# Revit family: BoelsRental_ScissorLift_JLG_1930ESa
name_source: partatom
category: Site
units: mm (PartAtom-declared; Revit-internal decimal feet)

## family parameters
Always vertical = Yes
Cut with Voids When Loaded = No
OmniClass Number = 23.50.05.14.11
OmniClass Title = Scissors Lifts
Part Type = Normal
Round Connector Dimension = Use Diameter
Shared = No
Work Plane-Based = No

## types (1)
- 1930ES
    Assembly Code = E1030100
    AssetType = Movable
    BIMObjectName = BoelsRental_ScissorLift_JLG_1930ES
    BoelsSubgroup = 12098 - Scissor lift 7.8m battery
    ClassificationName = Uniclass2015
    ClassificationValue = Pr_65_80_47_95
    Cost = 0 $
    DeepCycleBatteries = 220A-HR, 6V x4
    Description = SCISSOR LIFT, SELF-PROPELLED, PLATFORM WIDTH < 90 CM, ELEC. < 6 M
    DocumentationCertificates = https://www.boels.com
    DocumentationInstallationGuide = https://www.boels.com
    DocumentationLiterature = https://www.boels.com
    DocumentationMaintenance = https://www.boels.com
    DocumentationTechnical = https://www.boels.com
    Drive = 24V DC Shunt Wound
    DriveSpeedElevator = 0.98 kph (0.61 mph)
    DriveSpeedLowered = 4.90 kph (3.04 mph)
    DurationUnit = Years
    ExpectedLife = 0
    Gradeability = 25%
    GrossVehicleWeightANSI = 1327 kg (2925 lbs)
    GrossVehicleWeightCE = 1603kg (3535 lbs)
    GroundClearance = 0.089 m ( 0 ft 3.5 in)
    HydraulicSystem = 122 L (32 gal)
    IfcExportAs = IfcTransportElement
    IfcExportType = IfcTransportElementType
    Keynote = X
    LiftUpTime = 18 sec
    LowerDownTime = 22 sec
    Manufacturer = Boels Rental (JLG)
    ManufacturerName = Boels Rental (JLG)
    Material = Steel
    MaxGroundBearingPressureANSI = 8.73kg/cm2 (124.17 psi)
    MaxGroundBearingPressureCE = 8.73kg/cm2 (124.17 psi)
    Model = Scissor Lift - 1930ES
    ModelNumber = 1930ES
    ModelReference = Scissor Lift
    NBSDescription = Vertical lifting platforms
    NBSObjectName = Boels Rental - Vertical lifting platforms
    NBSReference = 90-80-65/350
    NominalDepth = 0 mm  [stored 0 ft]
    NominalHeight = 0 mm  [stored 0 ft]
    NominalLength = 0 mm  [stored 0 ft]
    PlatformCapacityANSI = 227 kg (500 lbs)
    PlatformCapacityCE = 227 kg (500 lbs)
    PlatformExtentionCapacityANSI = 113 kg (250 lbs)
    PlatformExtentionCapacityCE = 113 kg (250 lbs)
    PlatformExtentionSize = 0.96m (3 ft 2 in)
    PlatformSize = 0.76 m x 1.87 m (2 ft 6 in x 6 ft 2 in)
    ProductPageLink = https://www.boels.com
    ProductionYear = 2022
    RaisedPlatformHeight = 5.70 m (18 ft 8 in)
    Static = 583 mm
    TurningRadiusInside = 0 m
    TurningRadiusOutside = 1.75 m (5 ft 9 in)
    Type Comments = Scissor Lift - 1930ES
    TypeName = Scissor Lift - 1930ES
    URL = https://www.boels.com
    WarrantyDurationLabor = 0
    WarrantyDurationParts = 0
    WarrantyDurationUnit = Years
    WarrantyGuarantorLabor = https://www.boels.com
    WarrantyGuarantorParts = https://www.boels.com
    _BSBibleVersion = 16
    _BimSpecGuid = 0
    _CurrentRevision = 1
    _DistributedBy = https://www.boels.com
    _ObjectUserGuide = https://www.boels.com

note: [stored X ft] marks values corroborated as IEEE doubles in the binary element streams (Revit-internal decimal feet)

## geometry (parser evidence)
native form markers: Sweep x47
no freeform markers — native parametric forms only
